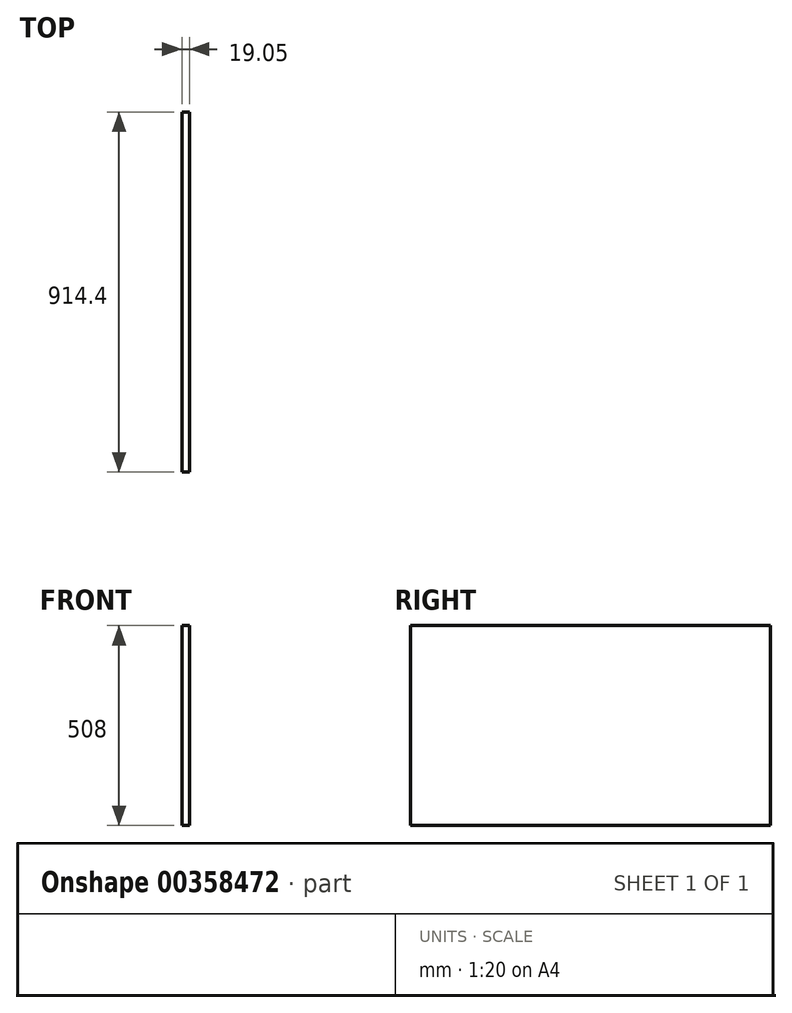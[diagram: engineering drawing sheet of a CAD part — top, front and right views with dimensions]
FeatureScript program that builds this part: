
annotation { "Feature Type Name" : "Feature", "Feature Type Description" : "" }
export const myFeature = defineFeature(function(context is Context, id is Id, definition is map)
    precondition{}
    {
        {
            var Q0;
            Q0=qCreatedBy(makeId("Right.planeOp"),FACE);
            var sketch = newSketch(context, id + "F0", { "sketchPlane" : qUnion([Q0])});
            skLineSegment(sketch, "E0.bottom", {"start": v(0, 0) * mm, "end": v(-914.4, 0) * mm});
            skLineSegment(sketch, "E0.top", {"start": v(0, -508) * mm, "end": v(-914.4, -508) * mm});
            skLineSegment(sketch, "E0.left", {"start": v(0, 0) * mm, "end": v(0, -508) * mm});
            skLineSegment(sketch, "E0.right", {"start": v(-914.4, 0) * mm, "end": v(-914.4, -508) * mm});
            skSolve(sketch);
        }
        {
            var Q0;
            Q0 = qSketchRegion(id + "F0", true);
            extrude(context, id + "F1", {"entities" : qUnion([Q0]), "depth" : 19.05 * mm});
        }
    });
